# Revit family: CC_Señal_Peligro
name_source: partatom
category: Generic Models
revit_build: Autodesk Revit 2018 (Build: 20190510_1515(x64)
units: mm (PartAtom-declared; Revit-internal decimal feet)

## family parameters
Always vertical = Yes
Can host rebar = No
Cut with Voids When Loaded = No
Part Type = Normal
Room Calculation Point = No
Round Connector Dimension = Use Diameter
Shared = No
Work Plane-Based = No

## types (6) — shared parameters
CC.Palo.Altura = 2200 mm
CC.Palo.Ancho = 100 mm  [stored 0.328084 ft]
CC.Palo.Profundidad = 50 mm  [stored 0.164042 ft]
CC.Panel.Altura = 1600 mm  [stored 5.24934 ft]

## per-type parameters (varying)
| type | Panel.Estado | Tipo.Panel |
| CC.Señal.Peligro | Panel.Blanco | CC_PanelPeligro : Panel.Definitivo.CruceIzq |
| CC.Señal.Prohibicion | Panel.Blanco | CC_PanelPeligro : Panel.Definitivo.CruceIzq |
| Senyal.Peligro.Cruce.Izq.Def | Panel.Blanco | CC_PanelPeligro : Panel.Definitivo.CruceIzq |
| Senyal.Peligro.Curv.Izq.Def | Panel.Blanco | CC_PanelPeligro : Panel.Definitivo.CurvaIzq |
| Senyal.Peligro.Cruce.Izq.Prov | Panel.Amarillo | CC_PanelPeligro : Panel.Definitivo.CruceIzq |
| Senyal.Peligro.Curv.Izq.Prov | Panel.Amarillo | CC_PanelPeligro : Panel.Definitivo.CurvaIzq |

note: [stored X ft] marks values corroborated as IEEE doubles in the binary element streams (Revit-internal decimal feet)

## geometry (parser evidence)
native form markers: Sweep x12
no freeform markers — native parametric forms only
